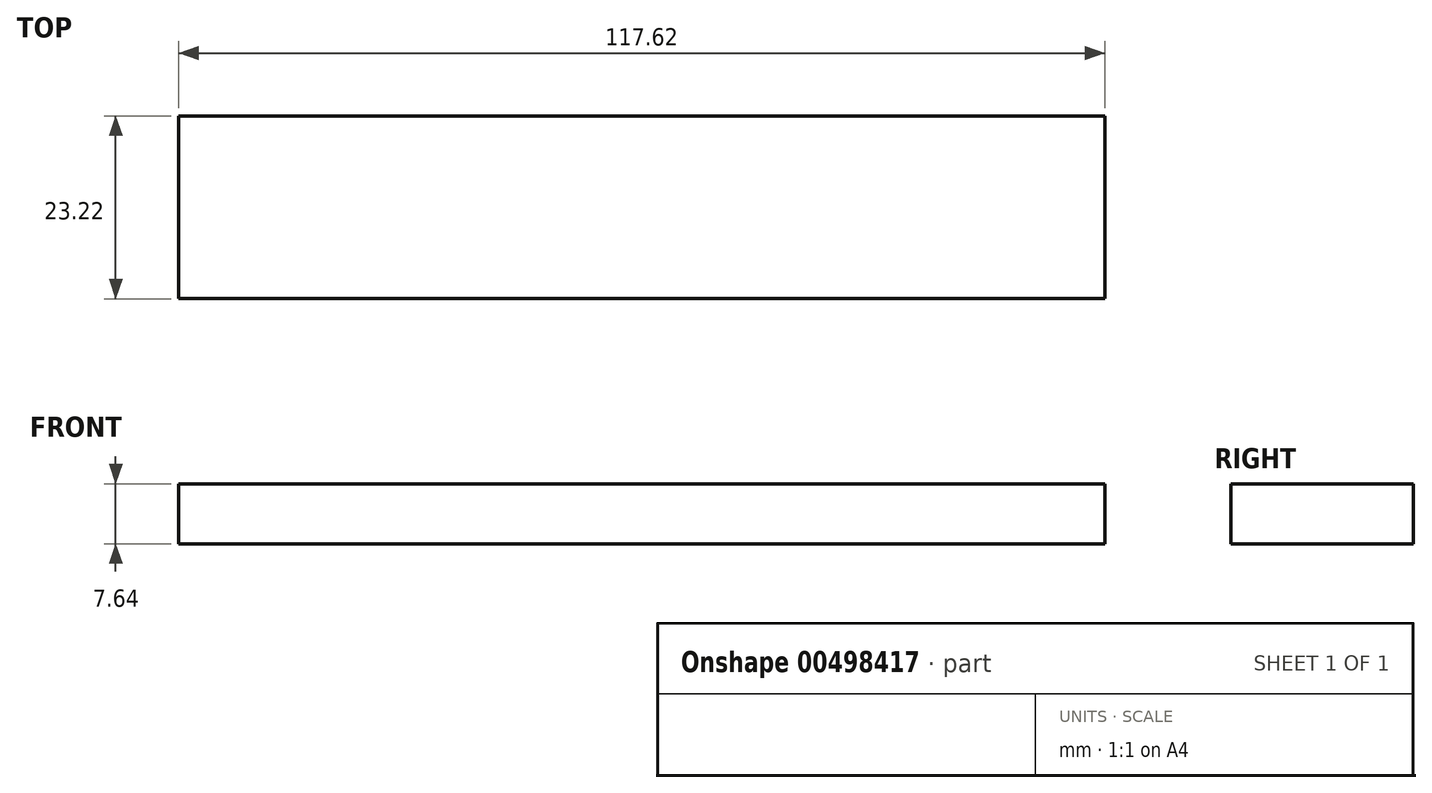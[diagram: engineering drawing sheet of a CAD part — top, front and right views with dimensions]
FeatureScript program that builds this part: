
annotation { "Feature Type Name" : "Feature", "Feature Type Description" : "" }
export const myFeature = defineFeature(function(context is Context, id is Id, definition is map)
    precondition{}
    {
        {
            var Q0;
            Q0=qCreatedBy(makeId("Top.planeOp"),FACE);
            var sketch = newSketch(context, id + "F0", { "sketchPlane" : qUnion([Q0])});
            skLineSegment(sketch, "E0.bottom", {"start": v(58.81, 11.6) * mm, "end": v(-58.81, 11.6) * mm});
            skLineSegment(sketch, "E0.top", {"start": v(58.81, -11.6) * mm, "end": v(-58.81, -11.6) * mm});
            skLineSegment(sketch, "E0.left", {"start": v(58.81, 11.6) * mm, "end": v(58.81, -11.6) * mm});
            skLineSegment(sketch, "E0.right", {"start": v(-58.81, 11.6) * mm, "end": v(-58.81, -11.6) * mm});
            skPoint(sketch, "E0.middle", {"position": v(0, 0) * mm});
            skSolve(sketch);
        }
        {
            var Q0;
            Q0=makeQuery(id+"F0.imprint","IMPRINT",FACE,{"disambiguationData":[TD([[makeQuery(id+"F0.imprint","IMPRINT",EDGE,{"derivedFrom":sQuery(id+"F0.wireOp",EDGE,"E0.bottom")}),1.0]])]});
            extrude(context, id + "F1", {"entities" : qUnion([Q0]), "depth" : 7.65 * mm, "symmetric" : true});
        }
    });
